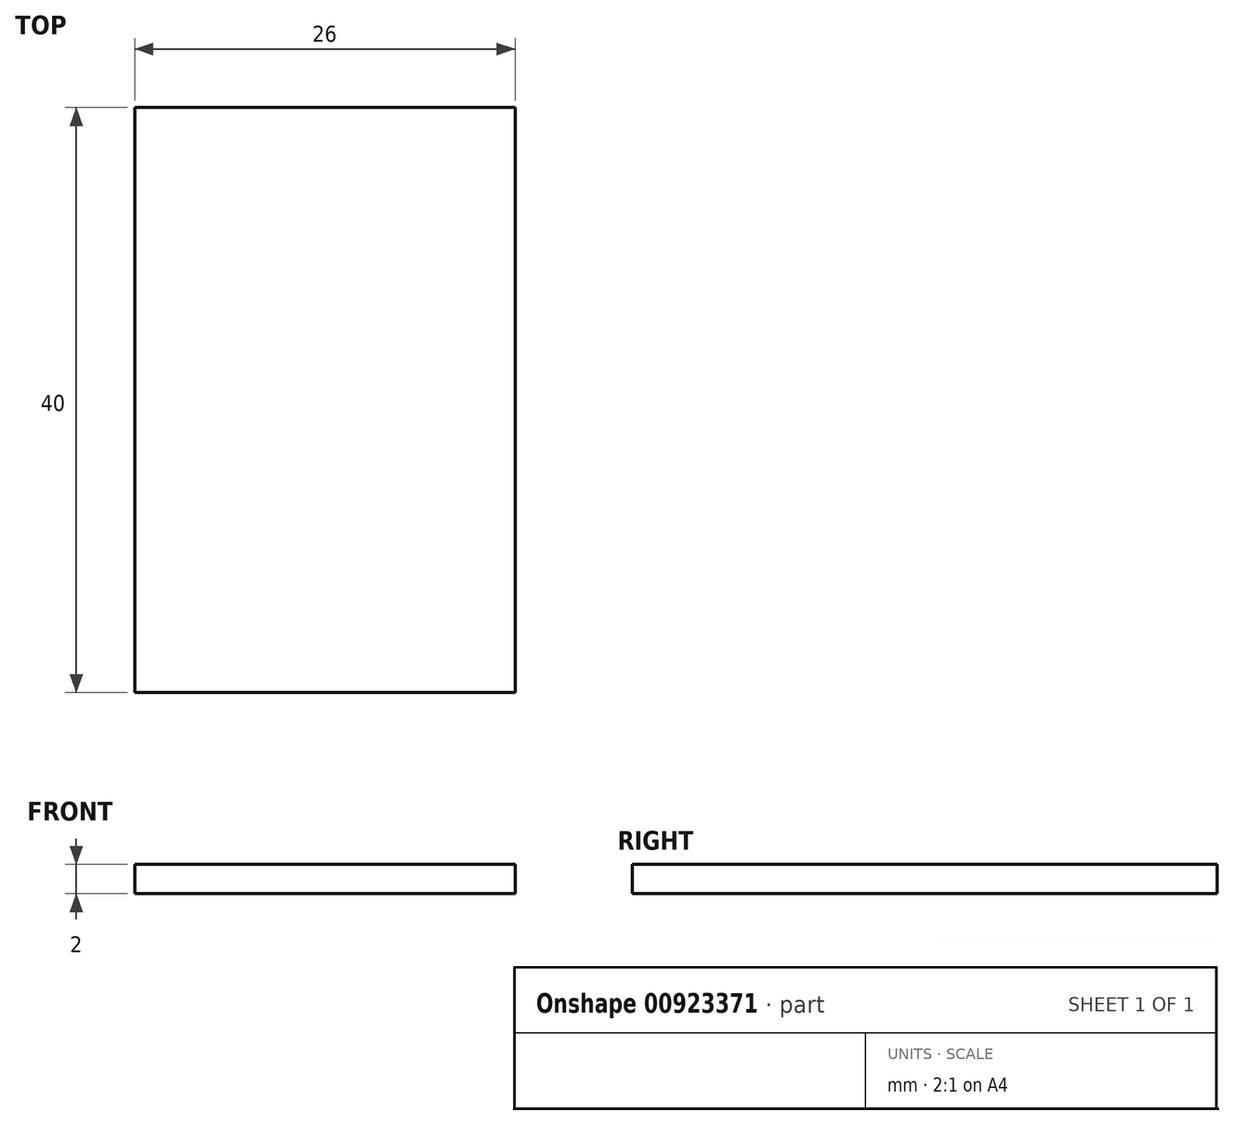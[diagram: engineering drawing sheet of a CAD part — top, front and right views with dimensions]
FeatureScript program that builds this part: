
annotation { "Feature Type Name" : "Feature", "Feature Type Description" : "" }
export const myFeature = defineFeature(function(context is Context, id is Id, definition is map)
    precondition{}
    {
        {
            var Q0;
            Q0=qCreatedBy(makeId("Top.planeOp"),FACE);
            var sketch = newSketch(context, id + "F0", { "sketchPlane" : qUnion([Q0])});
            skLineSegment(sketch, "E0.bottom", {"start": v(13, 20) * mm, "end": v(-13, 20) * mm});
            skLineSegment(sketch, "E0.top", {"start": v(13, -20) * mm, "end": v(-13, -20) * mm});
            skLineSegment(sketch, "E0.left", {"start": v(13, 20) * mm, "end": v(13, -20) * mm});
            skLineSegment(sketch, "E0.right", {"start": v(-13, 20) * mm, "end": v(-13, -20) * mm});
            skPoint(sketch, "E0.middle", {"position": v(0, 0) * mm});
            skSolve(sketch);
        }
        {
            var Q0;
            Q0=makeQuery(id+"F0.imprint","IMPRINT",FACE,{"disambiguationData":[TD([[makeQuery(id+"F0.imprint","IMPRINT",EDGE,{"derivedFrom":sQuery(id+"F0.wireOp",EDGE,"E0.bottom")}),1.0]])]});
            extrude(context, id + "F1", {"entities" : qUnion([Q0]), "depth" : 2 * mm, "offsetDistance" : 25 * mm});
        }
    });
